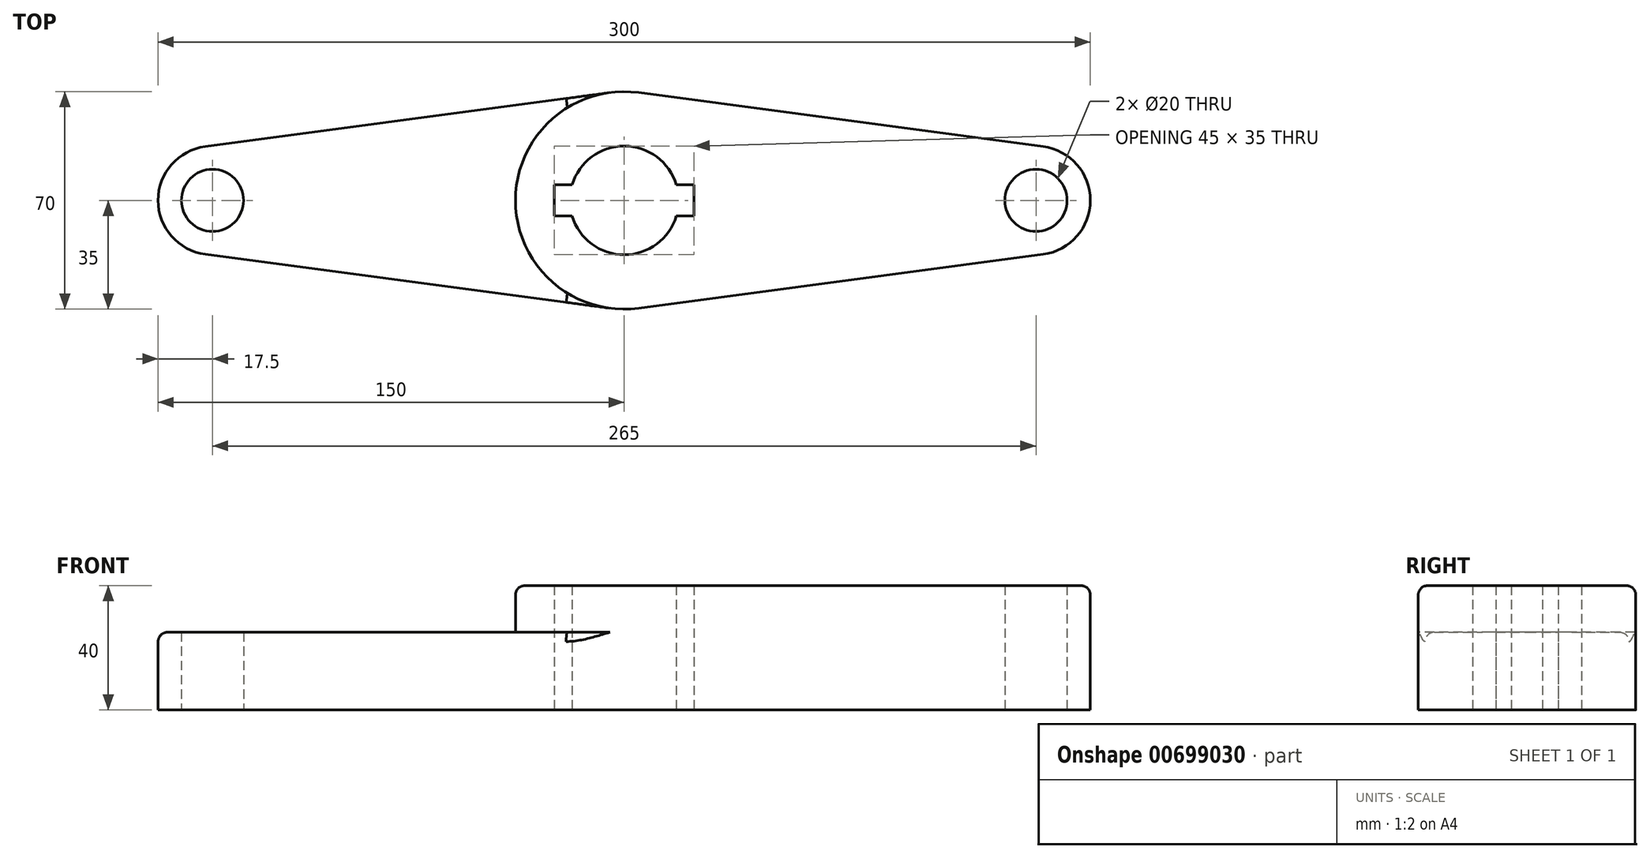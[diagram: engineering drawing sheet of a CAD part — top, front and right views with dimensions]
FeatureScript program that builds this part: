
annotation { "Feature Type Name" : "Feature", "Feature Type Description" : "" }
export const myFeature = defineFeature(function(context is Context, id is Id, definition is map)
    precondition{}
    {
        {
            var Q0;
            Q0=qCreatedBy(makeId("Top.planeOp"),FACE);
            var sketch = newSketch(context, id + "F0", { "sketchPlane" : qUnion([Q0])});
            skCircle(sketch, "E0", {"center": v(0, 0) * mm, "radius": 35 * mm});
            skCircle(sketch, "E1", {"center": v(132.5, 0) * mm, "radius": 17.5 * mm});
            skCircle(sketch, "E2", {"center": v(-132.5, 0) * mm, "radius": 17.5 * mm});
            skLineSegment(sketch, "E3", {"start": v(0, 0) * mm, "end": v(0, 79.73) * mm, "construction": true});
            skLineSegment(sketch, "E4", {"start": v(-134.81, 17.35) * mm, "end": v(-4.62, 34.7) * mm});
            skLineSegment(sketch, "E5", {"start": v(4.62, 34.7) * mm, "end": v(134.81, 17.35) * mm});
            skLineSegment(sketch, "E6", {"start": v(-4.62, -34.7) * mm, "end": v(-134.81, -17.35) * mm});
            skLineSegment(sketch, "E7", {"start": v(4.62, -34.7) * mm, "end": v(134.81, -17.35) * mm});
            skCircle(sketch, "E8", {"center": v(0, 0) * mm, "radius": 17.5 * mm});
            skCircle(sketch, "E9", {"center": v(-132.5, 0) * mm, "radius": 10 * mm});
            skCircle(sketch, "E10", {"center": v(132.5, 0) * mm, "radius": 10 * mm});
            skLineSegment(sketch, "E11.bottom", {"start": v(-22.5, 5) * mm, "end": v(22.5, 5) * mm});
            skLineSegment(sketch, "E11.top", {"start": v(-22.5, -5) * mm, "end": v(22.5, -5) * mm});
            skLineSegment(sketch, "E11.left", {"start": v(-22.5, 5) * mm, "end": v(-22.5, -5) * mm});
            skLineSegment(sketch, "E11.right", {"start": v(22.5, 5) * mm, "end": v(22.5, -5) * mm});
            skSolve(sketch);
        }
        {
            var Q0;
            {var subQ0=sQuery(id+"F0.wireOp",EDGE,"E5");Q0=makeQuery(id+"F0.imprint","IMPRINT",FACE,{"disambiguationData":[TD([[makeQuery(id+"F0.imprint","IMPRINT",EDGE,{"derivedFrom":subQ0}),-1.0]])]});}
            var Q1;
            {var subQ0=sQuery(id+"F0.wireOp",EDGE,"E11.left");Q1=makeQuery(id+"F0.imprint","IMPRINT",FACE,{"disambiguationData":[TD([[makeQuery(id+"F0.imprint","IMPRINT",EDGE,{"derivedFrom":subQ0}),-1.0]])]});}
            var Q2;
            Q2=makeQuery(id+"F0.imprint","IMPRINT",FACE,{"disambiguationData":[TD([[makeQuery(id+"F0.imprint","IMPRINT",EDGE,{"derivedFrom":sQuery(id+"F0.wireOp",EDGE,"E10")}),-1.0]])]});
            extrude(context, id + "F1", {"entities" : qUnion([Q0, Q1, Q2]), "depth" : 40 * mm});
        }
        {
            var Q0;
            {var subQ0=sQuery(id+"F0.wireOp",EDGE,"E4");Q0=makeQuery(id+"F0.imprint","IMPRINT",FACE,{"disambiguationData":[TD([[makeQuery(id+"F0.imprint","IMPRINT",EDGE,{"derivedFrom":subQ0}),-1.0]])]});}
            var Q1;
            Q1=makeQuery(id+"F0.imprint","IMPRINT",FACE,{"disambiguationData":[TD([[makeQuery(id+"F0.imprint","IMPRINT",EDGE,{"derivedFrom":sQuery(id+"F0.wireOp",EDGE,"E9")}),-1.0]])]});
            extrude(context, id + "F2", {"entities" : qUnion([Q0, Q1]), "operationType" : NewBodyOperationType.ADD, "depth" : 25 * mm});
        }
        {
            var Q0;
            Q0=makeQuery(id+"F2.opExtrude","CAP_EDGE",EDGE,{"disambiguationData":[OSD([sQuery(id+"F0.wireOp",EDGE,"E4")])],"isStart":false});
            var Q1;
            Q1=makeQuery(id+"F1.opExtrude","CAP_EDGE",EDGE,{"disambiguationData":[OSD([sQuery(id+"F0.wireOp",EDGE,"E0")])],"isStart":false});
            var Q2;
            Q2=makeQuery(id+"F2.opExtrude","CAP_EDGE",EDGE,{"disambiguationData":[OSD([sQuery(id+"F0.wireOp",EDGE,"E0")])],"isStart":false});
            fillet(context, id + "F3", {"entities" : qUnion([Q0, Q1, Q2]), "radius" : 3 * mm, "tangentPropagation" : true, "allowEdgeOverflow" : false});
        }
    });
